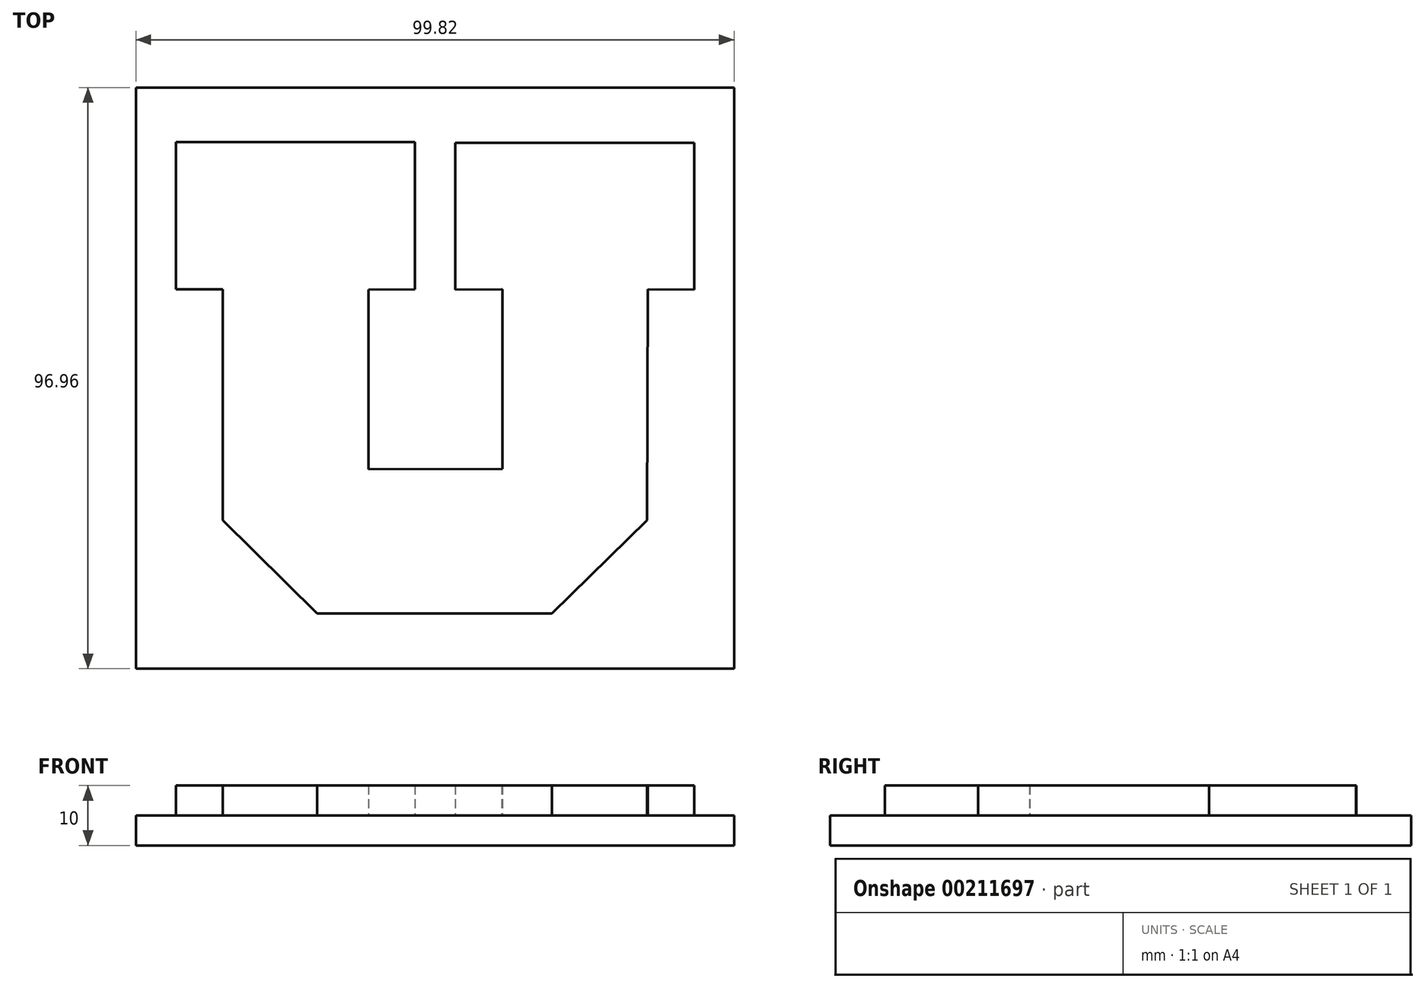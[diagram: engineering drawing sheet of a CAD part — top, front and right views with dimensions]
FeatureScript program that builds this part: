
annotation { "Feature Type Name" : "Feature", "Feature Type Description" : "" }
export const myFeature = defineFeature(function(context is Context, id is Id, definition is map)
    precondition{}
    {
        {
            assignVariable(context, id + "F0", {"name" : "thickness", "anyValue" : 5});
        }
        {
            var Q0;
            Q0=qCreatedBy(makeId("Top.planeOp"),FACE);
            var sketch = newSketch(context, id + "F1", { "sketchPlane" : qUnion([Q0])});
            skLineSegment(sketch, "E0.bottom", {"start": v(0, 0) * mm, "end": v(100, 0) * mm});
            skLineSegment(sketch, "E0.top", {"start": v(0, 100) * mm, "end": v(100, 100) * mm});
            skLineSegment(sketch, "E0.left", {"start": v(0, 0) * mm, "end": v(0, 100) * mm});
            skLineSegment(sketch, "E0.right", {"start": v(100, 0) * mm, "end": v(100, 100) * mm});
            skSolve(sketch);
        }
        {
            var Q0;
            Q0=makeQuery(id+"F1.imprint","IMPRINT",FACE,{"disambiguationData":[TD([[makeQuery(id+"F1.imprint","IMPRINT",EDGE,{"derivedFrom":sQuery(id+"F1.wireOp",EDGE,"E0.bottom")}),1.0]])]});
            extrude(context, id + "F2", {"entities" : qUnion([Q0]), "depth" : (getVariable(context, 'thickness')) * mm});
        }
        {
            var Q0;
            Q0=makeQuery(id+"F2.opExtrude","CAP_FACE",FACE,{"disambiguationData":[OSD([sQuery(id+"F1.wireOp",EDGE,"E0.bottom"),sQuery(id+"F1.wireOp",EDGE,"E0.top"),sQuery(id+"F1.wireOp",EDGE,"E0.left"),sQuery(id+"F1.wireOp",EDGE,"E0.right")])],"isStart":false});
            var sketch = newSketch(context, id + "F3", { "sketchPlane" : qUnion([Q0])});
            skLineSegment(sketch, "E1", {"start": v(6.67, 90.85) * mm, "end": v(0, 90.85) * mm});
            skLineSegment(sketch, "E2", {"start": v(93.16, 90.85) * mm, "end": v(100, 90.85) * mm});
            skSolve(sketch);
        }
        {
            var Q0;
            {var subQ3=makeQuery(id+"F2.opExtrude","CAP_EDGE",EDGE,{"disambiguationData":[OSD([sQuery(id+"F1.wireOp",EDGE,"E0.bottom")])],"isStart":false});Q0=makeQuery(id+"F3.imprint","IMPRINT",FACE,{"disambiguationData":[TD([[makeQuery(id+"F3.imprint","IMPRINT",EDGE,{"derivedFrom":subQ3}),1.0]])]});}
            var sketch = newSketch(context, id + "F4", { "sketchPlane" : qUnion([Q0])});
            skLineSegment(sketch, "E3", {"start": v(6.66, 90.9) * mm, "end": v(6.66, 66.35) * mm});
            skLineSegment(sketch, "E4", {"start": v(6.66, 66.35) * mm, "end": v(14.47, 66.35) * mm});
            skLineSegment(sketch, "E5", {"start": v(14.47, 66.35) * mm, "end": v(14.47, 27.78) * mm});
            skLineSegment(sketch, "E6", {"start": v(14.47, 27.78) * mm, "end": v(30.25, 12.22) * mm});
            skLineSegment(sketch, "E7", {"start": v(30.25, 12.22) * mm, "end": v(69.4, 12.22) * mm});
            skLineSegment(sketch, "E8", {"start": v(69.4, 12.22) * mm, "end": v(85.27, 27.78) * mm});
            skLineSegment(sketch, "E9", {"start": v(85.27, 27.78) * mm, "end": v(85.43, 66.35) * mm});
            skLineSegment(sketch, "E10", {"start": v(85.43, 66.35) * mm, "end": v(93.16, 66.32) * mm});
            skLineSegment(sketch, "E11", {"start": v(93.16, 66.32) * mm, "end": v(93.16, 90.82) * mm});
            skLineSegment(sketch, "E12", {"start": v(93.16, 90.82) * mm, "end": v(53.3, 90.82) * mm});
            skLineSegment(sketch, "E13", {"start": v(53.3, 90.82) * mm, "end": v(53.3, 66.32) * mm});
            skLineSegment(sketch, "E14", {"start": v(53.3, 66.32) * mm, "end": v(61.06, 66.35) * mm});
            skLineSegment(sketch, "E15", {"start": v(61.18, 36.4) * mm, "end": v(38.78, 36.31) * mm});
            skLineSegment(sketch, "E16", {"start": v(38.78, 36.31) * mm, "end": v(38.78, 66.32) * mm});
            skLineSegment(sketch, "E17", {"start": v(38.78, 66.32) * mm, "end": v(46.54, 66.35) * mm});
            skLineSegment(sketch, "E18", {"start": v(46.54, 66.35) * mm, "end": v(46.54, 90.82) * mm});
            skLineSegment(sketch, "E19", {"start": v(6.66, 90.9) * mm, "end": v(46.54, 90.9) * mm});
            skLineSegment(sketch, "E20", {"start": v(46.54, 90.9) * mm, "end": v(46.54, 90.82) * mm});
            skLineSegment(sketch, "E21", {"start": v(61.18, 36.4) * mm, "end": v(61.18, 66.35) * mm});
            skLineSegment(sketch, "E22", {"start": v(61.18, 66.35) * mm, "end": v(61.06, 66.35) * mm});
            skSolve(sketch);
        }
        {
            var Q0;
            Q0=makeQuery(id+"F4.imprint","IMPRINT",FACE,{"disambiguationData":[TD([[makeQuery(id+"F4.imprint","IMPRINT",EDGE,{"derivedFrom":sQuery(id+"F4.wireOp",EDGE,"E3")}),1.0]])]});
            var Q1;
            Q1 = qConstructionFilter(qBodyType(qCreatedBy(id + "F4" ,EDGE), BodyType.WIRE), ConstructionObject.NO);
            extrude(context, id + "F5", {"entities" : qUnion([Q0]), "surfaceEntities" : qUnion([Q1]), "depth" : (getVariable(context, 'thickness')) * mm});
        }
        {
            var Q0;
            Q0=makeQuery(id+"F5.opExtrude","CAP_FACE",FACE,{"disambiguationData":[OSD([sQuery(id+"F4.wireOp",EDGE,"E3"),sQuery(id+"F4.wireOp",EDGE,"E4"),sQuery(id+"F4.wireOp",EDGE,"E5"),sQuery(id+"F4.wireOp",EDGE,"E6"),sQuery(id+"F4.wireOp",EDGE,"E7"),sQuery(id+"F4.wireOp",EDGE,"E8"),sQuery(id+"F4.wireOp",EDGE,"E9"),sQuery(id+"F4.wireOp",EDGE,"E10"),sQuery(id+"F4.wireOp",EDGE,"E11"),sQuery(id+"F4.wireOp",EDGE,"E12"),sQuery(id+"F4.wireOp",EDGE,"E13"),sQuery(id+"F4.wireOp",EDGE,"E14"),sQuery(id+"F4.wireOp",EDGE,"E15"),sQuery(id+"F4.wireOp",EDGE,"E16"),sQuery(id+"F4.wireOp",EDGE,"E17"),sQuery(id+"F4.wireOp",EDGE,"E18"),sQuery(id+"F4.wireOp",EDGE,"E19"),sQuery(id+"F4.wireOp",EDGE,"E20"),sQuery(id+"F4.wireOp",EDGE,"E21"),sQuery(id+"F4.wireOp",EDGE,"E22")])],"isStart":false});
            var sketch = newSketch(context, id + "F6", { "sketchPlane" : qUnion([Q0])});
            skLineSegment(sketch, "E23", {"start": v(37.45, 12.22) * mm, "end": v(37.45, 3.04) * mm});
            skLineSegment(sketch, "E24.bottom", {"start": v(0, 0) * mm, "end": v(100.16, 0) * mm});
            skLineSegment(sketch, "E24.top", {"start": v(0, 3.04) * mm, "end": v(100.16, 3.04) * mm});
            skLineSegment(sketch, "E24.left", {"start": v(0, 0) * mm, "end": v(0, 3.04) * mm});
            skLineSegment(sketch, "E24.right", {"start": v(100.16, 0) * mm, "end": v(100.16, 3.04) * mm});
            skSolve(sketch);
        }
        {
            var Q0;
            Q0=makeQuery(id+"F6.imprint","IMPRINT",FACE,{"disambiguationData":[TD([[makeQuery(id+"F6.imprint","IMPRINT",EDGE,{"derivedFrom":sQuery(id+"F6.wireOp",EDGE,"E24.bottom")}),1.0]])]});
            extrude(context, id + "F7", {"entities" : qUnion([Q0]), "operationType" : NewBodyOperationType.REMOVE, "oppositeDirection" : true, "depth" : 54.1 * mm});
        }
        {
            var Q0;
            Q0=makeQuery(id+"F5.opExtrude","CAP_FACE",FACE,{"disambiguationData":[OSD([sQuery(id+"F4.wireOp",EDGE,"E3"),sQuery(id+"F4.wireOp",EDGE,"E4"),sQuery(id+"F4.wireOp",EDGE,"E5"),sQuery(id+"F4.wireOp",EDGE,"E6"),sQuery(id+"F4.wireOp",EDGE,"E7"),sQuery(id+"F4.wireOp",EDGE,"E8"),sQuery(id+"F4.wireOp",EDGE,"E9"),sQuery(id+"F4.wireOp",EDGE,"E10"),sQuery(id+"F4.wireOp",EDGE,"E11"),sQuery(id+"F4.wireOp",EDGE,"E12"),sQuery(id+"F4.wireOp",EDGE,"E13"),sQuery(id+"F4.wireOp",EDGE,"E14"),sQuery(id+"F4.wireOp",EDGE,"E15"),sQuery(id+"F4.wireOp",EDGE,"E16"),sQuery(id+"F4.wireOp",EDGE,"E17"),sQuery(id+"F4.wireOp",EDGE,"E18"),sQuery(id+"F4.wireOp",EDGE,"E19"),sQuery(id+"F4.wireOp",EDGE,"E20"),sQuery(id+"F4.wireOp",EDGE,"E21"),sQuery(id+"F4.wireOp",EDGE,"E22")])],"isStart":false});
            var sketch = newSketch(context, id + "F8", { "sketchPlane" : qUnion([Q0])});
            skLineSegment(sketch, "E25", {"start": v(93.16, 74.6) * mm, "end": v(99.82, 74.57) * mm});
            skLineSegment(sketch, "E26.bottom", {"start": v(99.82, 103.92) * mm, "end": v(108.06, 103.92) * mm});
            skLineSegment(sketch, "E26.top", {"start": v(99.82, -5.46) * mm, "end": v(108.06, -5.46) * mm});
            skLineSegment(sketch, "E26.left", {"start": v(99.82, 103.92) * mm, "end": v(99.82, -5.46) * mm});
            skLineSegment(sketch, "E26.right", {"start": v(108.06, 103.92) * mm, "end": v(108.06, -5.46) * mm});
            skSolve(sketch);
        }
        {
            var Q0;
            {var subQ3=sQuery(id+"F8.wireOp",EDGE,"E26.bottom");Q0=makeQuery(id+"F8.imprint","IMPRINT",FACE,{"disambiguationData":[TD([[makeQuery(id+"F8.imprint","IMPRINT",EDGE,{"derivedFrom":subQ3}),-1.0]])]});}
            extrude(context, id + "F9", {"entities" : qUnion([Q0]), "operationType" : NewBodyOperationType.REMOVE, "oppositeDirection" : true, "depth" : 25 * mm});
        }
    });
